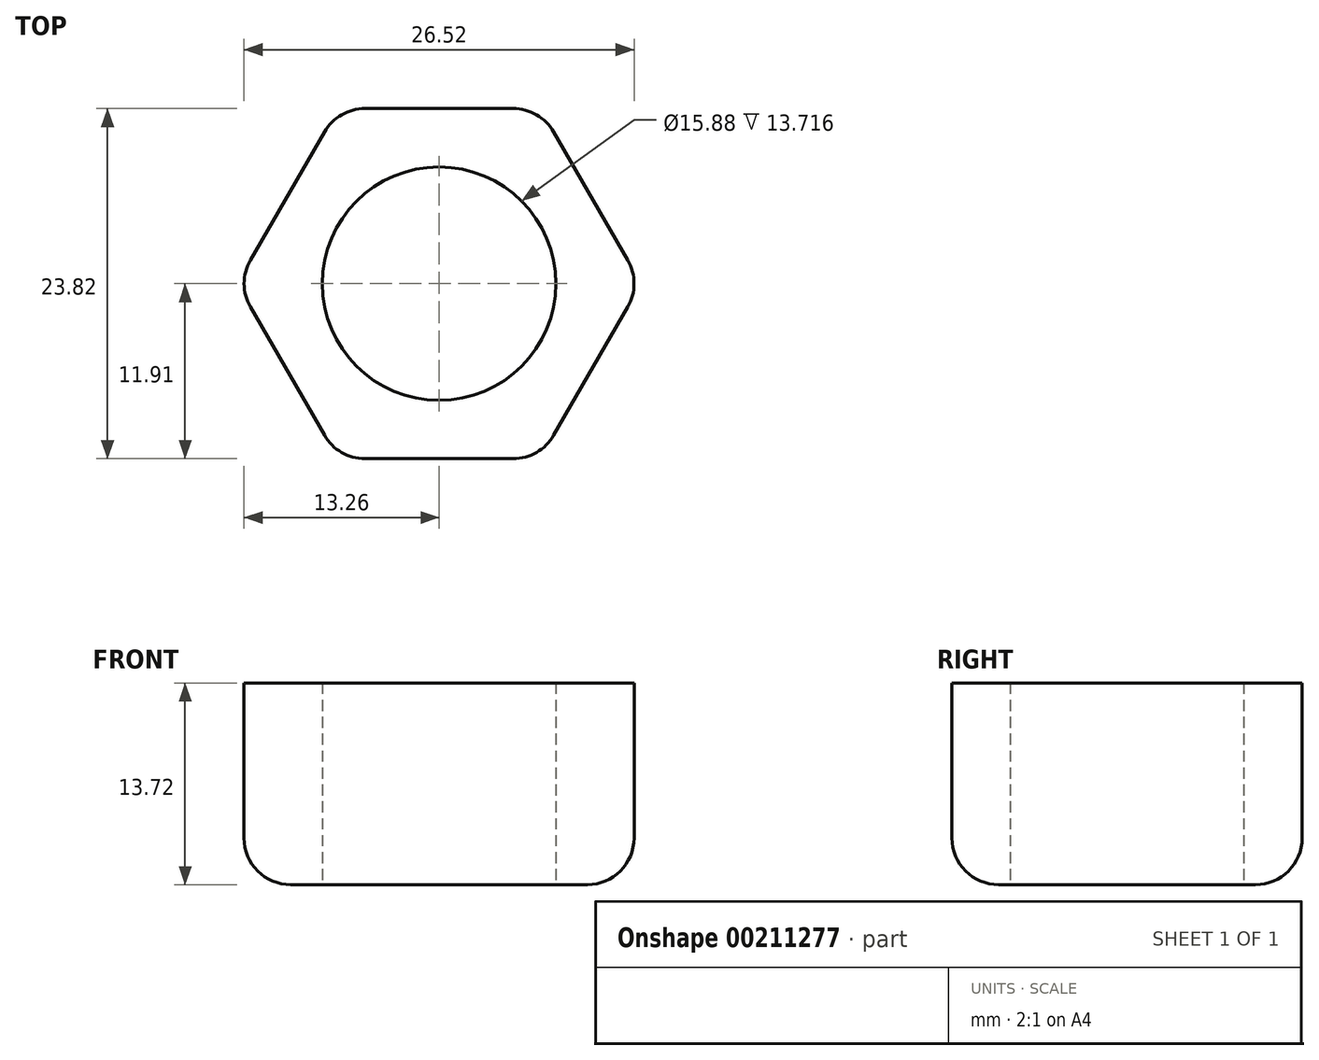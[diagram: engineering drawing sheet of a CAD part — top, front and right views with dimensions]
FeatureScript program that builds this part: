
annotation { "Feature Type Name" : "Feature", "Feature Type Description" : "" }
export const myFeature = defineFeature(function(context is Context, id is Id, definition is map)
    precondition{}
    {
        {
            var Q0;
            Q0=qCreatedBy(makeId("Top.planeOp"),FACE);
            var sketch = newSketch(context, id + "F0", { "sketchPlane" : qUnion([Q0])});
            skCircle(sketch, "E0.cCircle", {"center": v(0, 0) * mm, "radius": 11.9 * mm, "construction": true});
            skLineSegment(sketch, "E0.0", {"start": v(-6.87, 11.9) * mm, "end": v(6.87, 11.9) * mm});
            skLineSegment(sketch, "E0.1", {"start": v(6.87, 11.9) * mm, "end": v(13.75, 0) * mm});
            skLineSegment(sketch, "E0.2", {"start": v(13.75, 0) * mm, "end": v(6.87, -11.9) * mm});
            skLineSegment(sketch, "E0.3", {"start": v(6.87, -11.9) * mm, "end": v(-6.87, -11.9) * mm});
            skLineSegment(sketch, "E0.4", {"start": v(-6.87, -11.9) * mm, "end": v(-13.75, 0) * mm});
            skLineSegment(sketch, "E0.5", {"start": v(-13.75, 0) * mm, "end": v(-6.87, 11.9) * mm});
            skPoint(sketch, "E0.0.midPoint", {"position": v(0, 11.9) * mm});
            skCircle(sketch, "E1", {"center": v(0, 0) * mm, "radius": 7.94 * mm});
            skSolve(sketch);
        }
        {
            var Q0;
            Q0=qSketchRegion(id+"F0",true);
            extrude(context, id + "F1", {"entities" : qUnion([Q0]), "depth" : 13.72 * mm});
        }
        {
            var Q0;
            Q0=makeQuery(id+"F1.opExtrude","SWEPT_EDGE",EDGE,{"disambiguationData":[OSD([sQuery(id+"F0.wireOp",EDGE,"E0.4"),sQuery(id+"F0.wireOp",EDGE,"E0.5")])]});
            var Q1;
            Q1=makeQuery(id+"F1.opExtrude","CAP_EDGE",EDGE,{"disambiguationData":[OSD([sQuery(id+"F0.wireOp",EDGE,"E0.2")])],"isStart":true});
            var Q2;
            Q2=makeQuery(id+"F1.opExtrude","SWEPT_EDGE",EDGE,{"disambiguationData":[OSD([sQuery(id+"F0.wireOp",EDGE,"E0.1"),sQuery(id+"F0.wireOp",EDGE,"E0.2")])]});
            var Q3;
            Q3=makeQuery(id+"F1.opExtrude","SWEPT_EDGE",EDGE,{"disambiguationData":[OSD([sQuery(id+"F0.wireOp",EDGE,"E0.2"),sQuery(id+"F0.wireOp",EDGE,"E0.3")])]});
            var Q4;
            Q4=makeQuery(id+"F1.opExtrude","SWEPT_EDGE",EDGE,{"disambiguationData":[OSD([sQuery(id+"F0.wireOp",EDGE,"E0.3"),sQuery(id+"F0.wireOp",EDGE,"E0.4")])]});
            var Q5;
            Q5=makeQuery(id+"F1.opExtrude","SWEPT_EDGE",EDGE,{"disambiguationData":[OSD([sQuery(id+"F0.wireOp",EDGE,"E0.0"),sQuery(id+"F0.wireOp",EDGE,"E0.1")])]});
            var Q6;
            Q6=makeQuery(id+"F1.opExtrude","SWEPT_EDGE",EDGE,{"disambiguationData":[OSD([sQuery(id+"F0.wireOp",EDGE,"E0.0"),sQuery(id+"F0.wireOp",EDGE,"E0.5")])]});
            var Q7;
            Q7=makeQuery(id+"F1.opExtrude","CAP_EDGE",EDGE,{"disambiguationData":[OSD([sQuery(id+"F0.wireOp",EDGE,"E0.3")])],"isStart":true});
            var Q8;
            Q8=makeQuery(id+"F1.opExtrude","CAP_EDGE",EDGE,{"disambiguationData":[OSD([sQuery(id+"F0.wireOp",EDGE,"E0.4")])],"isStart":true});
            var Q9;
            Q9=makeQuery(id+"F1.opExtrude","CAP_EDGE",EDGE,{"disambiguationData":[OSD([sQuery(id+"F0.wireOp",EDGE,"E0.5")])],"isStart":true});
            var Q10;
            Q10=makeQuery(id+"F1.opExtrude","CAP_EDGE",EDGE,{"disambiguationData":[OSD([sQuery(id+"F0.wireOp",EDGE,"E0.0")])],"isStart":true});
            var Q11;
            Q11=makeQuery(id+"F1.opExtrude","CAP_EDGE",EDGE,{"disambiguationData":[OSD([sQuery(id+"F0.wireOp",EDGE,"E0.1")])],"isStart":true});
            fillet(context, id + "F2", {"entities" : qUnion([Q0, Q1, Q2, Q3, Q4, Q5, Q6, Q7, Q8, Q9, Q10, Q11]), "radius" : 3.17 * mm, "tangentPropagation" : true, "allowEdgeOverflow" : false});
        }
    });
